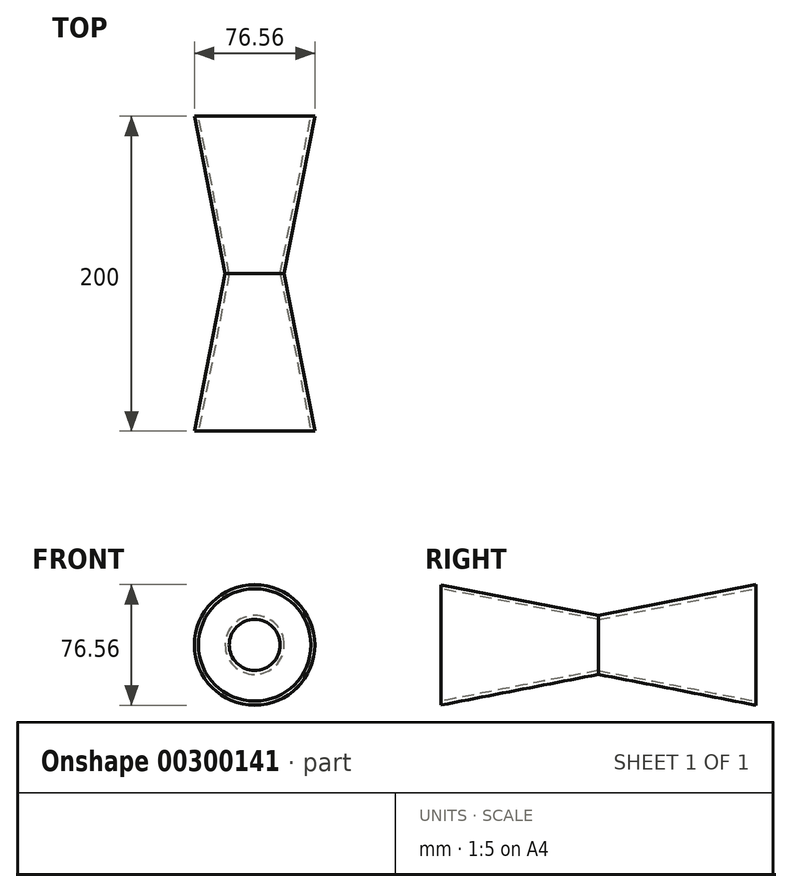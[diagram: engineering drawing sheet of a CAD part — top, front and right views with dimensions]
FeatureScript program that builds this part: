
annotation { "Feature Type Name" : "Feature", "Feature Type Description" : "" }
export const myFeature = defineFeature(function(context is Context, id is Id, definition is map)
    precondition{}
    {
        {
            var Q0;
            Q0=qCreatedBy(makeId("Front.planeOp"),FACE);
            var sketch = newSketch(context, id + "F0", { "sketchPlane" : qUnion([Q0])});
            skCircle(sketch, "E0", {"center": v(0, 0) * mm, "radius": 38.28 * mm});
            skSolve(sketch);
        }
        {
            var Q0;
            Q0=qCreatedBy(makeId("Front.planeOp"),FACE);
            cPlane(context, id + "F1", {"entities" : qUnion([Q0]), "cplaneType" : CPlaneType.OFFSET, "offset" : 100 * mm, "width" : 152.4 * mm, "height" : 152.4 * mm});
        }
        {
            var Q0;
            Q0=qCreatedBy(id+"F1.planeOp",FACE);
            var sketch = newSketch(context, id + "F2", { "sketchPlane" : qUnion([Q0])});
            skCircle(sketch, "E1", {"center": v(0, 0) * mm, "radius": 18.73 * mm});
            skSolve(sketch);
        }
        {
            var Q0;
            Q0=makeQuery(id+"F0.imprint","IMPRINT",FACE,{"disambiguationData":[TD([[makeQuery(id+"F0.imprint","IMPRINT",EDGE,{"derivedFrom":sQuery(id+"F0.wireOp",EDGE,"E0")}),1.0]])]});
            var Q1;
            Q1=makeQuery(id+"F2.imprint","IMPRINT",FACE,{"disambiguationData":[TD([[makeQuery(id+"F2.imprint","IMPRINT",EDGE,{"derivedFrom":sQuery(id+"F2.wireOp",EDGE,"E1")}),1.0]])]});
            loft(context, id + "F3", {"sheetProfilesArray" : [{ "sheetProfileEntities" : qUnion([Q0]) }, { "sheetProfileEntities" : qUnion([Q1]) }]});
        }
        {
            var Q0;
            Q0=qCreatedBy(id+"F1.planeOp",FACE);
            cPlane(context, id + "F4", {"entities" : qUnion([Q0]), "cplaneType" : CPlaneType.OFFSET, "offset" : 100 * mm, "width" : 150 * mm, "height" : 150 * mm});
        }
        {
            var Q0;
            Q0=qCreatedBy(id+"F4.planeOp",FACE);
            var sketch = newSketch(context, id + "F5", { "sketchPlane" : qUnion([Q0])});
            skCircle(sketch, "E2", {"center": v(0, 0) * mm, "radius": 38.25 * mm});
            skSolve(sketch);
        }
        {
            var Q1;
            Q1=makeQuery(id+"F5.imprint","IMPRINT",FACE,{"disambiguationData":[TD([[makeQuery(id+"F5.imprint","IMPRINT",EDGE,{"derivedFrom":sQuery(id+"F5.wireOp",EDGE,"E2")}),1.0]])]});
            var Q2;
            Q2=makeQuery(id+"F3.opLoft","CAP_FACE",FACE,{"disambiguationData":[OSD([makeQuery(id+"F2.imprint","IMPRINT",FACE,{"disambiguationData":[TD([[makeQuery(id+"F2.imprint","IMPRINT",EDGE,{"derivedFrom":sQuery(id+"F2.wireOp",EDGE,"E1")}),1.0]])]})])],"isStart":true});
            loft(context, id + "F6", {"operationType" : NewBodyOperationType.ADD, "sheetProfilesArray" : [{ "sheetProfileEntities" : qUnion([Q1]) }, { "sheetProfileEntities" : qUnion([Q2]) }]});
        }
        {
            var Q0;
            Q0=makeQuery(id+"F6.opLoft","CAP_FACE",FACE,{"disambiguationData":[OSD([makeQuery(id+"F5.imprint","IMPRINT",FACE,{"disambiguationData":[TD([[makeQuery(id+"F5.imprint","IMPRINT",EDGE,{"derivedFrom":sQuery(id+"F5.wireOp",EDGE,"E2")}),1.0]])]})])],"isStart":true});
            var Q1;
            Q1=makeQuery(id+"F3.opLoft","CAP_FACE",FACE,{"disambiguationData":[OSD([makeQuery(id+"F0.imprint","IMPRINT",FACE,{"disambiguationData":[TD([[makeQuery(id+"F0.imprint","IMPRINT",EDGE,{"derivedFrom":sQuery(id+"F0.wireOp",EDGE,"E0")}),1.0]])]})])],"isStart":true});
            shell(context, id + "F7", {"entities" : qUnion([Q0, Q1]), "thickness" : 2.5 * mm});
        }
    });
